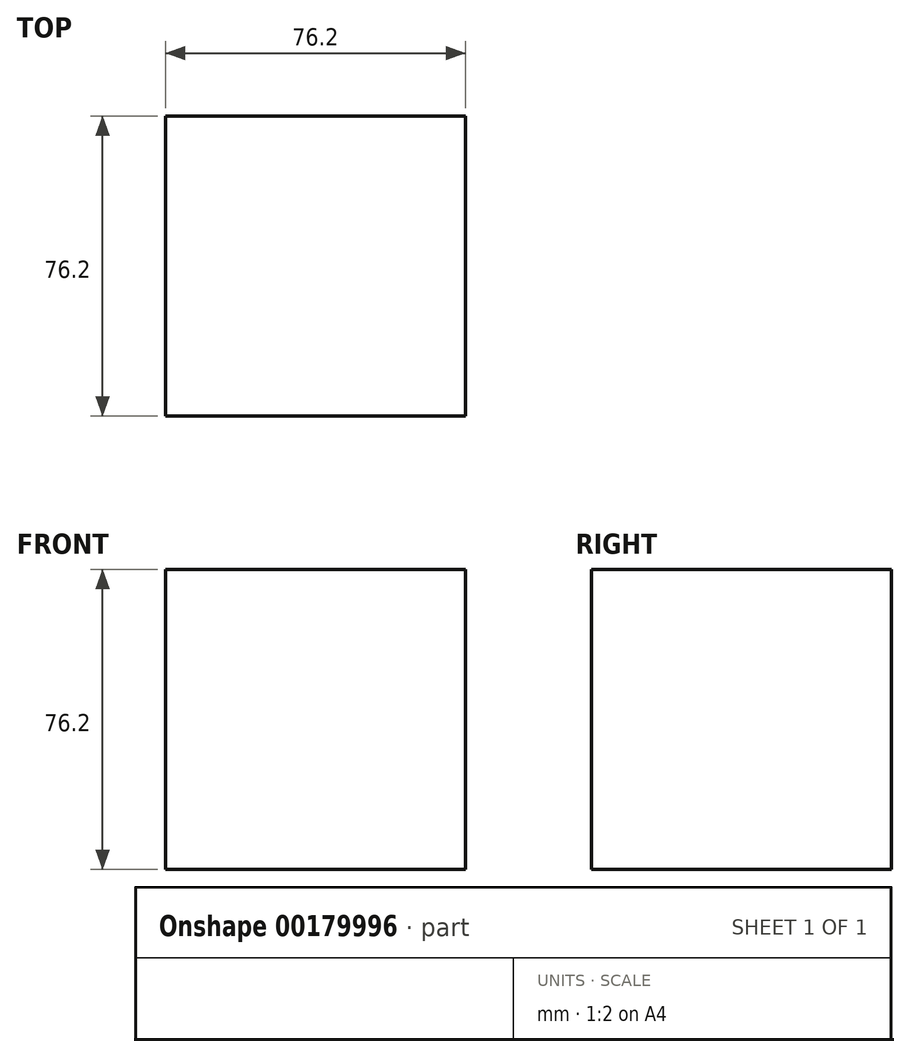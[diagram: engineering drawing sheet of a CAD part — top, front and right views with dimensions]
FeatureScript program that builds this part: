
annotation { "Feature Type Name" : "Feature", "Feature Type Description" : "" }
export const myFeature = defineFeature(function(context is Context, id is Id, definition is map)
    precondition{}
    {
        {
            var Q0;
            Q0=qCreatedBy(makeId("Right.planeOp"),FACE);
            var sketch = newSketch(context, id + "F0", { "sketchPlane" : qUnion([Q0])});
            skLineSegment(sketch, "E0.bottom", {"start": v(-38.1, 38.1) * mm, "end": v(38.1, 38.1) * mm});
            skLineSegment(sketch, "E0.top", {"start": v(-38.1, -38.1) * mm, "end": v(38.1, -38.1) * mm});
            skLineSegment(sketch, "E0.left", {"start": v(-38.1, 38.1) * mm, "end": v(-38.1, -38.1) * mm});
            skLineSegment(sketch, "E0.right", {"start": v(38.1, 38.1) * mm, "end": v(38.1, -38.1) * mm});
            skPoint(sketch, "E0.middle", {"position": v(0, 0) * mm});
            skSolve(sketch);
        }
        {
            var Q0;
            Q0 = qSketchRegion(id + "F0", true);
            extrude(context, id + "F1", {"entities" : qUnion([Q0]), "depth" : 76.2 * mm});
        }
    });
